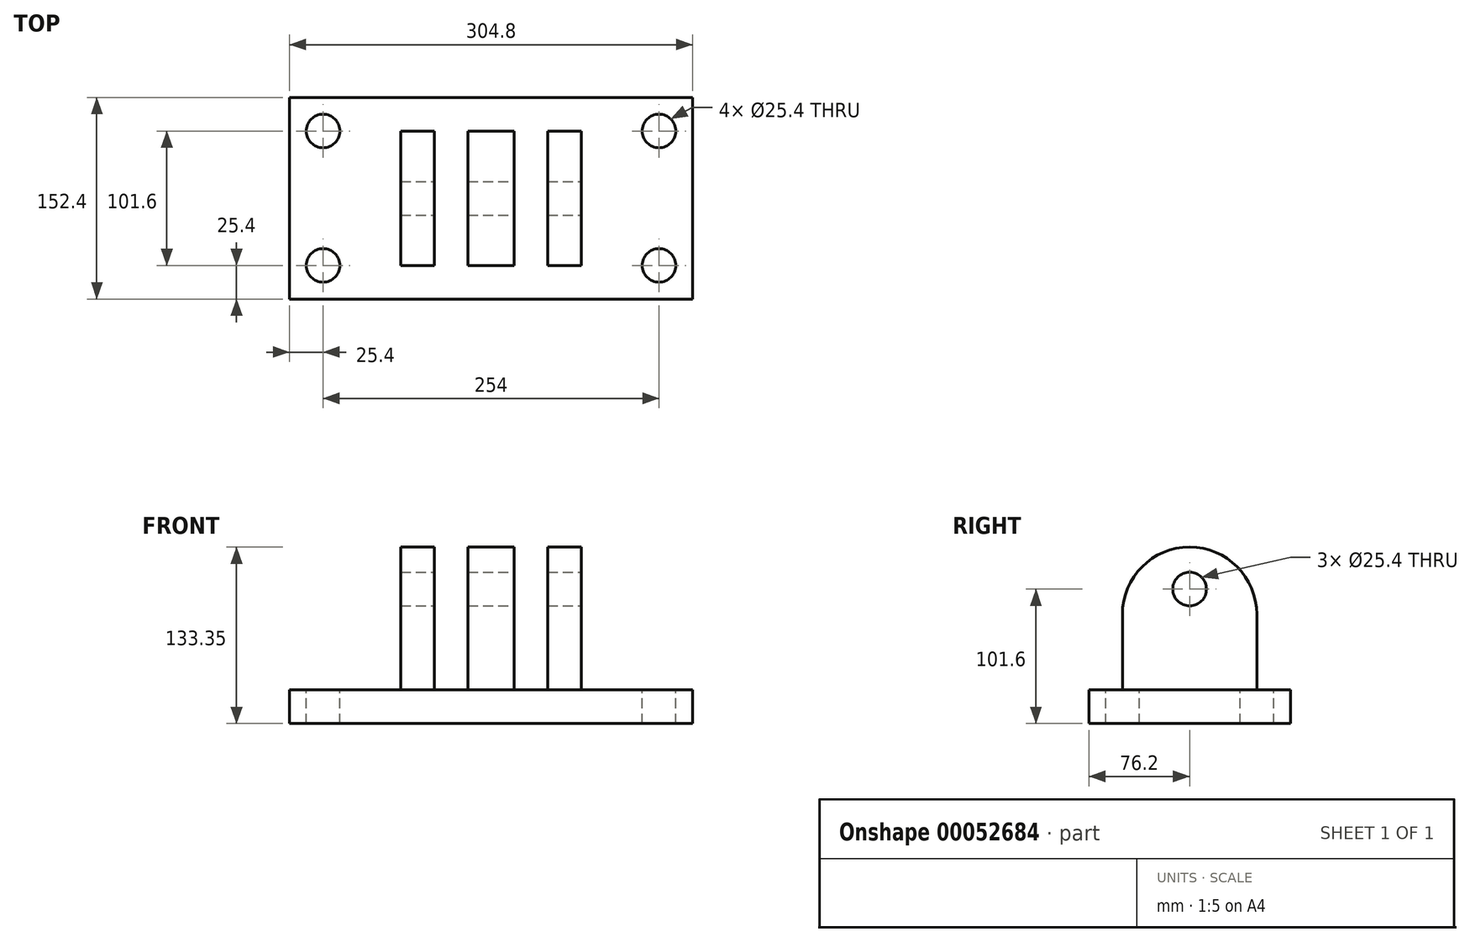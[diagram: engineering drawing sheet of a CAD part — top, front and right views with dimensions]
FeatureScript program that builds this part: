
annotation { "Feature Type Name" : "Feature", "Feature Type Description" : "" }
export const myFeature = defineFeature(function(context is Context, id is Id, definition is map)
    precondition{}
    {
        {
            var Q0;
            Q0=qCreatedBy(makeId("Top.planeOp"),FACE);
            var sketch = newSketch(context, id + "F0", { "sketchPlane" : qUnion([Q0])});
            skLineSegment(sketch, "E0.rect.bottom", {"start": v(152.4, 76.2) * mm, "end": v(-152.4, 76.2) * mm});
            skLineSegment(sketch, "E0.rect.top", {"start": v(152.4, -76.2) * mm, "end": v(-152.4, -76.2) * mm});
            skLineSegment(sketch, "E0.rect.left", {"start": v(152.4, 76.2) * mm, "end": v(152.4, -76.2) * mm});
            skLineSegment(sketch, "E0.rect.right", {"start": v(-152.4, 76.2) * mm, "end": v(-152.4, -76.2) * mm});
            skPoint(sketch, "E0.rect.middle", {"position": v(0, 0) * mm});
            skLineSegment(sketch, "E1.rect.bottom", {"start": v(-17.46, -50.8) * mm, "end": v(17.46, -50.8) * mm});
            skLineSegment(sketch, "E1.rect.top", {"start": v(-17.46, 50.8) * mm, "end": v(17.46, 50.8) * mm});
            skLineSegment(sketch, "E1.rect.left", {"start": v(-17.46, -50.8) * mm, "end": v(-17.46, 50.8) * mm});
            skLineSegment(sketch, "E1.rect.right", {"start": v(17.46, -50.8) * mm, "end": v(17.46, 50.8) * mm});
            skLineSegment(sketch, "E2.rect.right", {"start": v(68.26, -50.8) * mm, "end": v(68.26, 50.8) * mm});
            skLineSegment(sketch, "E2.rect.left", {"start": v(42.86, -50.8) * mm, "end": v(42.86, 50.8) * mm});
            skLineSegment(sketch, "E2.rect.top", {"start": v(42.86, 50.8) * mm, "end": v(68.26, 50.8) * mm});
            skLineSegment(sketch, "E2.rect.bottom", {"start": v(42.86, -50.8) * mm, "end": v(68.26, -50.8) * mm});
            skLineSegment(sketch, "E3.rect.right", {"start": v(-42.86, -50.8) * mm, "end": v(-42.86, 50.8) * mm});
            skLineSegment(sketch, "E3.rect.left", {"start": v(-68.26, -50.8) * mm, "end": v(-68.26, 50.8) * mm});
            skLineSegment(sketch, "E3.rect.top", {"start": v(-68.26, 50.8) * mm, "end": v(-42.86, 50.8) * mm});
            skLineSegment(sketch, "E3.rect.bottom", {"start": v(-68.26, -50.8) * mm, "end": v(-42.86, -50.8) * mm});
            skLineSegment(sketch, "E4.rect.bottom", {"start": v(127, 50.8) * mm, "end": v(-127, 50.8) * mm, "construction": true});
            skLineSegment(sketch, "E4.rect.top", {"start": v(127, -50.8) * mm, "end": v(-127, -50.8) * mm, "construction": true});
            skLineSegment(sketch, "E4.rect.left", {"start": v(127, 50.8) * mm, "end": v(127, -50.8) * mm, "construction": true});
            skLineSegment(sketch, "E4.rect.right", {"start": v(-127, 50.8) * mm, "end": v(-127, -50.8) * mm, "construction": true});
            skPoint(sketch, "E5", {"position": v(127, 50.8) * mm});
            skPoint(sketch, "E6", {"position": v(-127, 50.8) * mm});
            skPoint(sketch, "E7", {"position": v(-127, -50.8) * mm});
            skPoint(sketch, "E8", {"position": v(127, -50.8) * mm});
            skSolve(sketch);
        }
        {
            var Q0;
            Q0=makeQuery(id+"F0.imprint","IMPRINT",FACE,{"disambiguationData":[TD([[makeQuery(id+"F0.imprint","IMPRINT",EDGE,{"derivedFrom":sQuery(id+"F0.wireOp",EDGE,"E3.rect.right")}),1.0]])]});
            var Q1;
            Q1=makeQuery(id+"F0.imprint","IMPRINT",FACE,{"disambiguationData":[TD([[makeQuery(id+"F0.imprint","IMPRINT",EDGE,{"derivedFrom":sQuery(id+"F0.wireOp",EDGE,"E2.rect.right")}),1.0]])]});
            var Q2;
            Q2=makeQuery(id+"F0.imprint","IMPRINT",FACE,{"disambiguationData":[TD([[makeQuery(id+"F0.imprint","IMPRINT",EDGE,{"derivedFrom":sQuery(id+"F0.wireOp",EDGE,"E1.rect.bottom")}),1.0]])]});
            var Q3;
            Q3=makeQuery(id+"F0.imprint","IMPRINT",FACE,{"disambiguationData":[TD([[makeQuery(id+"F0.imprint","IMPRINT",EDGE,{"derivedFrom":sQuery(id+"F0.wireOp",EDGE,"E0.rect.bottom")}),1.0]])]});
            extrude(context, id + "F1", {"entities" : qUnion([Q0, Q1, Q2, Q3]), "oppositeDirection" : true, "depth" : 25.4 * mm});
        }
        {
            var Q0;
            Q0=makeQuery(id+"F0.imprint","IMPRINT",FACE,{"disambiguationData":[TD([[makeQuery(id+"F0.imprint","IMPRINT",EDGE,{"derivedFrom":sQuery(id+"F0.wireOp",EDGE,"E2.rect.right")}),1.0]])]});
            var Q1;
            Q1=makeQuery(id+"F0.imprint","IMPRINT",FACE,{"disambiguationData":[TD([[makeQuery(id+"F0.imprint","IMPRINT",EDGE,{"derivedFrom":sQuery(id+"F0.wireOp",EDGE,"E1.rect.bottom")}),1.0]])]});
            var Q2;
            Q2=makeQuery(id+"F0.imprint","IMPRINT",FACE,{"disambiguationData":[TD([[makeQuery(id+"F0.imprint","IMPRINT",EDGE,{"derivedFrom":sQuery(id+"F0.wireOp",EDGE,"E3.rect.right")}),1.0]])]});
            extrude(context, id + "F2", {"entities" : qUnion([Q0, Q1, Q2]), "operationType" : NewBodyOperationType.ADD, "depth" : 107.95 * mm});
        }
        {
            var Q0;
            Q0=makeQuery(id+"F2.opExtrude","SWEPT_FACE",FACE,{"disambiguationData":[OSD([sQuery(id+"F0.wireOp",EDGE,"E2.rect.right")])]});
            var sketch = newSketch(context, id + "F3", { "sketchPlane" : qUnion([Q0])});
            skLineSegment(sketch, "E9.0", {"start": v(-50.8, 107.95) * mm, "end": v(50.8, 107.95) * mm});
            skLineSegment(sketch, "E10.0", {"start": v(50.8, 107.95) * mm, "end": v(50.8, 0) * mm});
            skCircle(sketch, "E11", {"center": v(0, 76.2) * mm, "radius": 12.7 * mm});
            skLineSegment(sketch, "E12", {"start": v(0, 0) * mm, "end": v(0, 76.2) * mm, "construction": true});
            skLineSegment(sketch, "E13", {"start": v(0, 107.95) * mm, "end": v(0, 57.15) * mm, "construction": true});
            skPoint(sketch, "E14", {"position": v(0, 57.15) * mm});
            skArc(sketch, "E15", {"start": v(50.8, 57.15) * mm, "mid": v(0, 107.95) * mm, "end": v(-50.8, 57.15) * mm});
            skSolve(sketch);
        }
        {
            var Q0;
            {var subQ0=sQuery(id+"F3.wireOp",EDGE,"E10.0");var subQ1=sQuery(id+"F3.wireOp",EDGE,"E9.0");var subQ2=makeQuery(id+"F3.imprint","INTERSECT",VERTEX,{"derivedFrom":[subQ1,subQ0]});Q0=makeQuery(id+"F3.imprint","IMPRINT",FACE,{"disambiguationData":[TD([[makeQuery(id+"F3.imprint","IMPRINT",EDGE,{"disambiguationData":[TD([[subQ2,1.0]])],"derivedFrom":subQ1}),-1.0]])]});}
            var Q1;
            {var subQ0=sQuery(id+"F3.wireOp",EDGE,"E9.0");var subQ3=sQuery(id+"F3.wireOp",EDGE,"abcff7dd-9036-4236-953f-1920783a81b8");var subQ4=makeQuery(id+"F3.imprint","INTERSECT",VERTEX,{"derivedFrom":[subQ0,subQ3]});Q1=makeQuery(id+"F3.imprint","IMPRINT",FACE,{"disambiguationData":[TD([[makeQuery(id+"F3.imprint","IMPRINT",EDGE,{"disambiguationData":[TD([[subQ4,1.0]])],"derivedFrom":subQ0}),-1.0]])]});}
            extrude(context, id + "F4", {"entities" : qUnion([Q0, Q1]), "operationType" : NewBodyOperationType.REMOVE, "endBound" : BoundingType.THROUGH_ALL, "oppositeDirection" : true, "depth" : 25.4 * mm});
        }
        {
            var Q0;
            Q0=makeQuery(id+"F3.imprint","IMPRINT",FACE,{"disambiguationData":[TD([[makeQuery(id+"F3.imprint","IMPRINT",EDGE,{"derivedFrom":sQuery(id+"F3.wireOp",EDGE,"E11")}),1.0]])]});
            extrude(context, id + "F5", {"entities" : qUnion([Q0]), "operationType" : NewBodyOperationType.REMOVE, "endBound" : BoundingType.THROUGH_ALL, "oppositeDirection" : true, "depth" : 25.4 * mm});
        }
        {
            var Q0;
            Q0=sQuery(id+"F0.wireOp",VERTEX,"E4.rect.left.end");
            var Q1;
            Q1=sQuery(id+"F0.wireOp",VERTEX,"E5");
            var Q2;
            Q2=sQuery(id+"F0.wireOp",VERTEX,"E4.rect.right.start");
            var Q3;
            Q3=sQuery(id+"F0.wireOp",VERTEX,"E7");
            var Q4;
            Q4=makeQuery(id+"F1.opExtrude","SWEPT_BODY",BODY,{"disambiguationData":[OSD([sQuery(id+"F0.wireOp",EDGE,"E0.rect.bottom"),sQuery(id+"F0.wireOp",EDGE,"E0.rect.top"),sQuery(id+"F0.wireOp",EDGE,"E0.rect.left"),sQuery(id+"F0.wireOp",EDGE,"E0.rect.right")])]});
            hole(context, id + "F6", {"style" : HoleStyle.SIMPLE, "holeDiameter" : 25.4 * mm, "endStyle" : HoleEndStyle.THROUGH, "locations" : qUnion([Q0, Q1, Q2, Q3]), "scope" : qUnion([Q4])});
        }
    });
